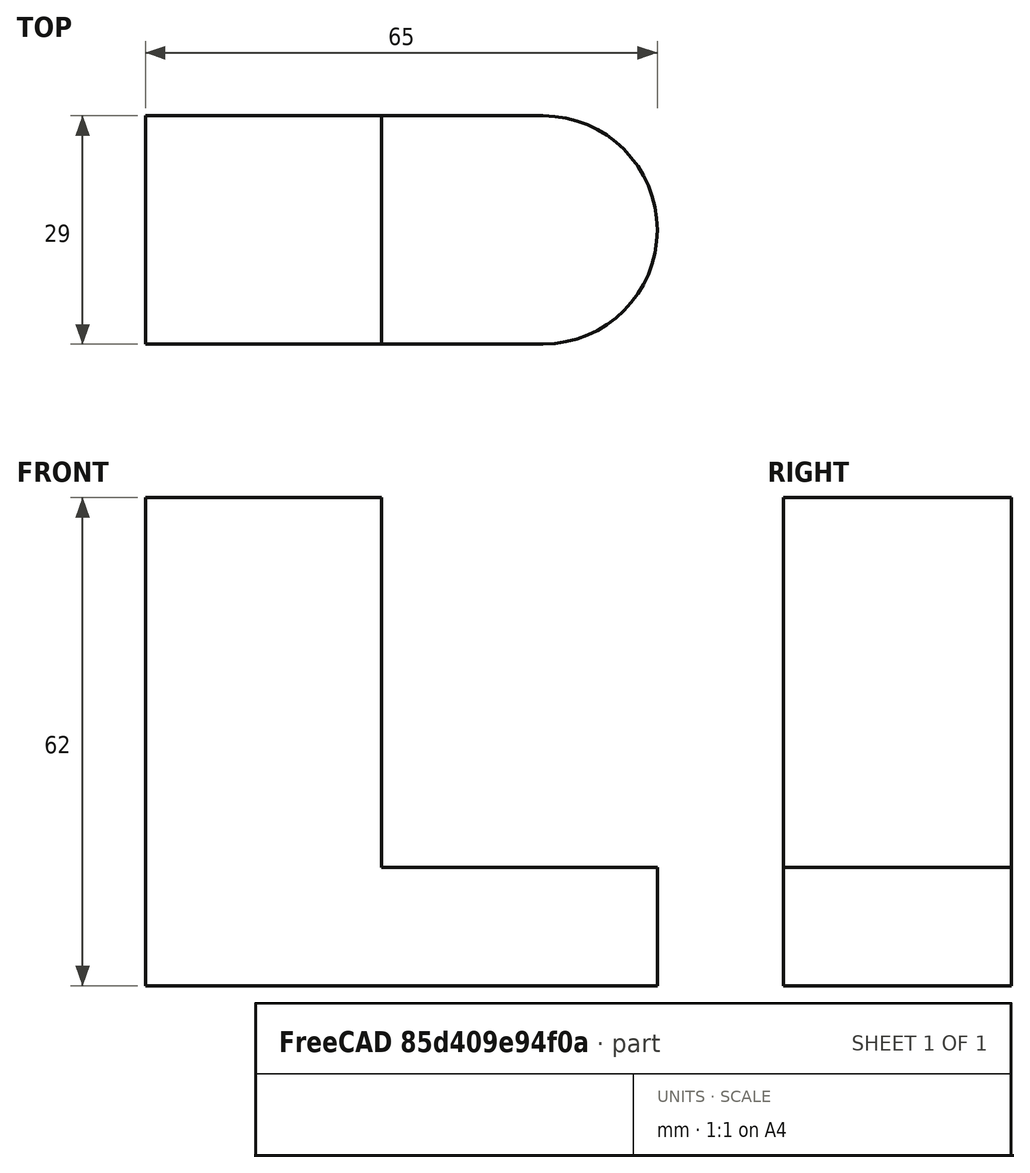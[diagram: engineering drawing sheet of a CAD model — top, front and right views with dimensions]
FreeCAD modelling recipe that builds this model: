
FCSTD DOCUMENT  (FreeCAD 1.0R39319 (Git))
Label: Challenge24-01-01
License: All rights reserved
LicenseURL: https://en.wikipedia.org/wiki/All_rights_reserved
objects: Sketcher::SketchObject×2, PartDesign::Pad×2, PartDesign::Body×1
note: 11 computed .brp shape members not serialized (recipe doc carries the construction recipe); baked Part::Feature solids carry a one-line shape summary decoded from their .brp

FEATURE [Sketcher::SketchObject] Sketch
  ArcFitTolerance = 1e-06
  AttachmentSupport = -> [XY_Plane]
  FullyConstrained = false
  MakeInternals = false
  MapMode = 5
  sketch-geometry (8):
    g0: LineSegment StartX=0 StartY=0 StartZ=0 EndX=50.5 EndY=0 EndZ=0
    g1: LineSegment StartX=65 StartY=14.5 StartZ=0 EndX=65 EndY=14.5 EndZ=0
    g2: LineSegment StartX=50.5 StartY=29 StartZ=0 EndX=0 EndY=29 EndZ=0
    g3: LineSegment StartX=0 StartY=29 StartZ=0 EndX=0 EndY=0 EndZ=0
    g4: ArcOfCircle CenterX=50.5 CenterY=14.5 CenterZ=0 NormalX=0 NormalY=0 NormalZ=1 AngleXU=0 Radius=14.5 StartAngle=0 EndAngle=1.5708
    g5: GeomPoint [constr] X=65 Y=29 Z=0
    g6: ArcOfCircle CenterX=50.5 CenterY=14.5 CenterZ=0 NormalX=0 NormalY=0 NormalZ=1 AngleXU=0 Radius=14.5 StartAngle=4.71239 EndAngle=6.28319
    g7: GeomPoint [constr] X=65 Y=0 Z=0
FEATURE [PartDesign::Pad] Pad
  Direction = (0,0,1)
  Length = 15
  Length2 = 10
  Profile = -> Sketch
  ReferenceAxis = -> Sketch [N_Axis]
  Refine = true
  Suppressed = false
  Type = 0
FEATURE [Sketcher::SketchObject] Sketch001
  ArcFitTolerance = 1e-06
  AttachmentSupport = -> [Pad]
  ExternalGeometry = -> [Pad]
  FullyConstrained = true
  MakeInternals = false
  MapMode = 5
  Placement = pos=(0,0,0) rot=(1,0,0;3.14159rad)
  sketch-geometry (4):
    g0: LineSegment StartX=0 StartY=0 StartZ=0 EndX=0 EndY=-29 EndZ=0
    g1: LineSegment StartX=0 StartY=-29 StartZ=0 EndX=30 EndY=-29 EndZ=0
    g2: LineSegment StartX=30 StartY=-29 StartZ=0 EndX=30 EndY=0 EndZ=0
    g3: LineSegment StartX=30 StartY=0 StartZ=0 EndX=0 EndY=0 EndZ=0
  constraints (11):
    c: Coincident(g0,g1)
    c: Coincident(g1,g2)
    c: Coincident(g2,g3)
    c: Coincident(g3,g0)
    c: Vertical(g0)
    c: Vertical(g2)
    c: Horizontal(g1)
    c: Horizontal(g3)
    c: Coincident(g0,g-1)
    c: PointOnObject(g1,g-3)
    c: Distance(g0,g2) = 30
FEATURE [PartDesign::Pad] Pad001
  BaseFeature = -> Pad
  Direction = (0,0,-1)
  Length = 62
  Length2 = 10
  Profile = -> Sketch001
  ReferenceAxis = -> Sketch001 [N_Axis]
  Refine = true
  Reversed = true
  Suppressed = false
  Type = 0
FEATURE [PartDesign::Body] Body
  AllowCompound = false
  Group = -> [Sketch,Pad,Sketch001,Pad001]
  Origin = -> Origin
  Tip = -> Pad001
